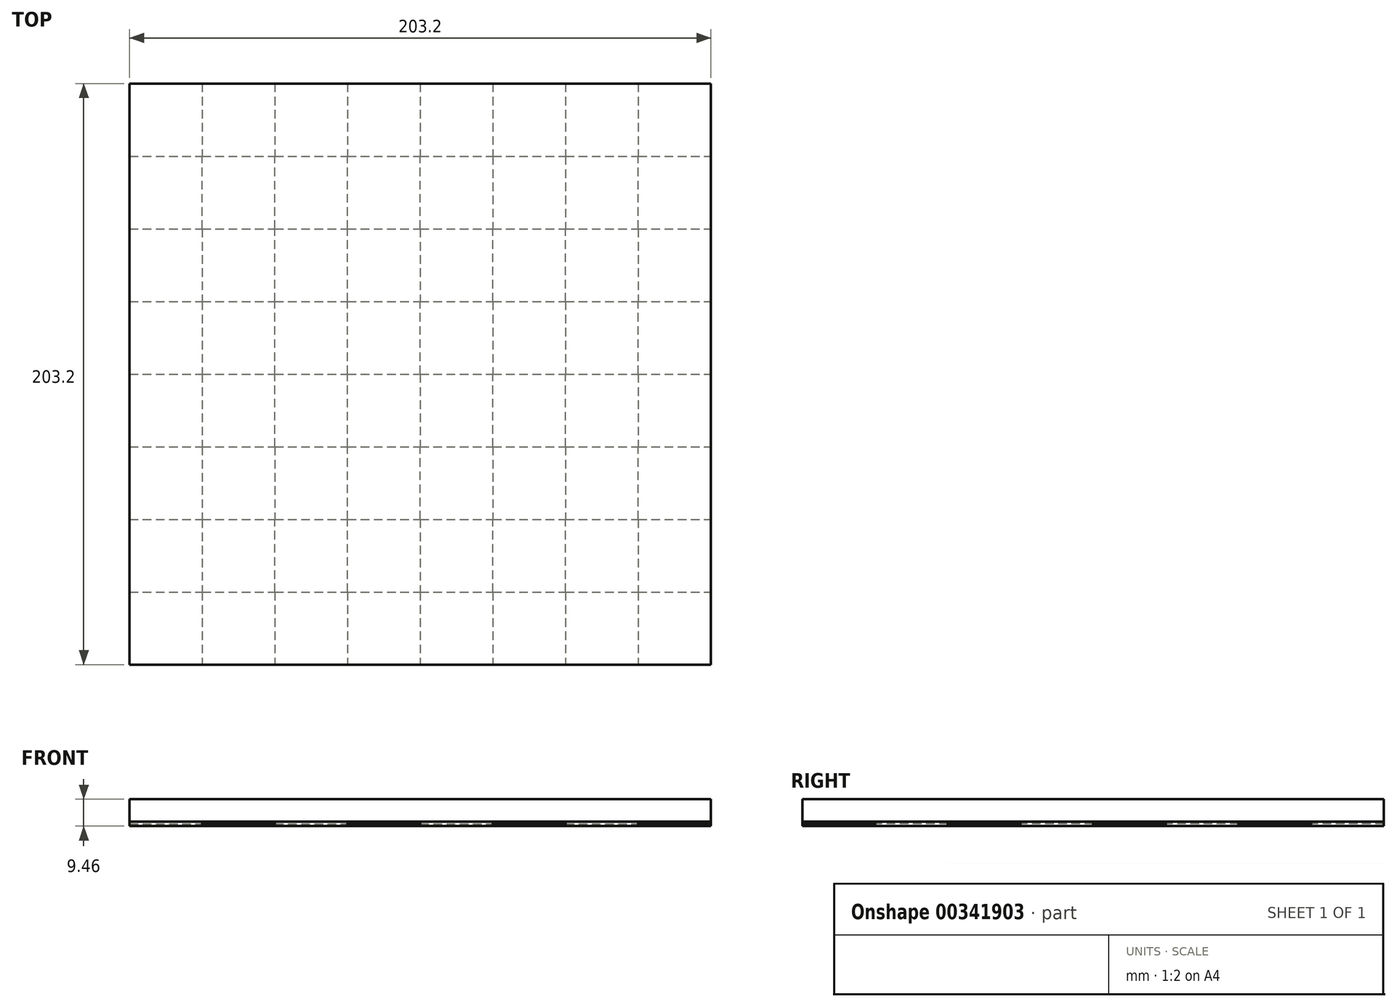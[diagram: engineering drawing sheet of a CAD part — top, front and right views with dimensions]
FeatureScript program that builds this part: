
annotation { "Feature Type Name" : "Feature", "Feature Type Description" : "" }
export const myFeature = defineFeature(function(context is Context, id is Id, definition is map)
    precondition{}
    {
        {
            var Q0;
            Q0=qCreatedBy(makeId("Top.planeOp"),FACE);
            var sketch = newSketch(context, id + "F0", { "sketchPlane" : qUnion([Q0])});
            skLineSegment(sketch, "E0.bottom", {"start": v(-101.6, -101.6) * mm, "end": v(101.6, -101.6) * mm});
            skLineSegment(sketch, "E0.top", {"start": v(-101.6, 101.6) * mm, "end": v(101.6, 101.6) * mm});
            skLineSegment(sketch, "E0.left", {"start": v(-101.6, -101.6) * mm, "end": v(-101.6, 101.6) * mm});
            skLineSegment(sketch, "E0.right", {"start": v(101.6, -101.6) * mm, "end": v(101.6, 101.6) * mm});
            skLineSegment(sketch, "E1.0", {"start": v(-76.2, -101.6) * mm, "end": v(-76.2, 101.6) * mm});
            skLineSegment(sketch, "E2.0", {"start": v(-50.8, -101.6) * mm, "end": v(-50.8, 101.6) * mm});
            skLineSegment(sketch, "E3.0", {"start": v(-25.4, -101.6) * mm, "end": v(-25.4, 101.6) * mm});
            skLineSegment(sketch, "E4.0", {"start": v(0, -101.6) * mm, "end": v(0, 101.6) * mm});
            skLineSegment(sketch, "E5.0", {"start": v(25.4, -101.6) * mm, "end": v(25.4, 101.6) * mm});
            skLineSegment(sketch, "E6.0", {"start": v(50.8, -101.6) * mm, "end": v(50.8, 101.6) * mm});
            skLineSegment(sketch, "E7.0", {"start": v(76.2, -101.6) * mm, "end": v(76.2, 101.6) * mm});
            skLineSegment(sketch, "E8.0", {"start": v(-101.6, 76.2) * mm, "end": v(101.6, 76.2) * mm});
            skLineSegment(sketch, "E9.0", {"start": v(-101.6, 50.8) * mm, "end": v(101.6, 50.8) * mm});
            skLineSegment(sketch, "E10.0", {"start": v(-101.6, 25.4) * mm, "end": v(101.6, 25.4) * mm});
            skLineSegment(sketch, "E11.0", {"start": v(-101.6, 0) * mm, "end": v(101.6, 0) * mm});
            skLineSegment(sketch, "E12.0", {"start": v(-101.6, -25.4) * mm, "end": v(101.6, -25.4) * mm});
            skLineSegment(sketch, "E13.0", {"start": v(-101.6, -50.8) * mm, "end": v(101.6, -50.8) * mm});
            skLineSegment(sketch, "E14.0", {"start": v(-101.6, -76.2) * mm, "end": v(101.6, -76.2) * mm});
            skSolve(sketch);
        }
        {
            var Q0;
            {var subQ0=sQuery(id+"F0.wireOp",EDGE,"E0.right");var subQ1=sQuery(id+"F0.wireOp",EDGE,"E0.top");var subQ2=makeQuery(id+"F0.imprint","INTERSECT",VERTEX,{"derivedFrom":[subQ1,subQ0]});Q0=makeQuery(id+"F0.imprint","IMPRINT",FACE,{"disambiguationData":[TD([[makeQuery(id+"F0.imprint","IMPRINT",EDGE,{"disambiguationData":[TD([[subQ2,1.0]])],"derivedFrom":subQ1}),-1.0]])]});}
            var Q1;
            {var subQ0=sQuery(id+"F0.wireOp",EDGE,"E9.0");var subQ1=sQuery(id+"F0.wireOp",EDGE,"E6.0");var subQ2=makeQuery(id+"F0.imprint","INTERSECT",VERTEX,{"derivedFrom":[subQ1,subQ0]});Q1=makeQuery(id+"F0.imprint","IMPRINT",FACE,{"disambiguationData":[TD([[makeQuery(id+"F0.imprint","IMPRINT",EDGE,{"disambiguationData":[TD([[subQ2,-1.0]])],"derivedFrom":subQ1}),-1.0]])]});}
            var Q2;
            {var subQ0=sQuery(id+"F0.wireOp",EDGE,"E5.0");var subQ1=sQuery(id+"F0.wireOp",EDGE,"E0.top");var subQ2=makeQuery(id+"F0.imprint","INTERSECT",VERTEX,{"derivedFrom":[subQ1,subQ0]});Q2=makeQuery(id+"F0.imprint","IMPRINT",FACE,{"disambiguationData":[TD([[makeQuery(id+"F0.imprint","IMPRINT",EDGE,{"disambiguationData":[TD([[subQ2,-1.0]])],"derivedFrom":subQ1}),-1.0]])]});}
            var Q3;
            {var subQ0=sQuery(id+"F0.wireOp",EDGE,"E3.0");var subQ1=sQuery(id+"F0.wireOp",EDGE,"E0.top");var subQ2=makeQuery(id+"F0.imprint","INTERSECT",VERTEX,{"derivedFrom":[subQ1,subQ0]});Q3=makeQuery(id+"F0.imprint","IMPRINT",FACE,{"disambiguationData":[TD([[makeQuery(id+"F0.imprint","IMPRINT",EDGE,{"disambiguationData":[TD([[subQ2,-1.0]])],"derivedFrom":subQ1}),-1.0]])]});}
            var Q4;
            {var subQ0=sQuery(id+"F0.wireOp",EDGE,"E9.0");var subQ1=sQuery(id+"F0.wireOp",EDGE,"E4.0");var subQ2=makeQuery(id+"F0.imprint","INTERSECT",VERTEX,{"derivedFrom":[subQ1,subQ0]});Q4=makeQuery(id+"F0.imprint","IMPRINT",FACE,{"disambiguationData":[TD([[makeQuery(id+"F0.imprint","IMPRINT",EDGE,{"disambiguationData":[TD([[subQ2,-1.0]])],"derivedFrom":subQ1}),-1.0]])]});}
            var Q5;
            {var subQ0=sQuery(id+"F0.wireOp",EDGE,"E1.0");var subQ1=sQuery(id+"F0.wireOp",EDGE,"E0.top");var subQ2=makeQuery(id+"F0.imprint","INTERSECT",VERTEX,{"derivedFrom":[subQ1,subQ0]});Q5=makeQuery(id+"F0.imprint","IMPRINT",FACE,{"disambiguationData":[TD([[makeQuery(id+"F0.imprint","IMPRINT",EDGE,{"disambiguationData":[TD([[subQ2,-1.0]])],"derivedFrom":subQ1}),-1.0]])]});}
            var Q6;
            {var subQ0=sQuery(id+"F0.wireOp",EDGE,"E8.0");var subQ1=sQuery(id+"F0.wireOp",EDGE,"E0.left");var subQ2=makeQuery(id+"F0.imprint","INTERSECT",VERTEX,{"derivedFrom":[subQ1,subQ0]});Q6=makeQuery(id+"F0.imprint","IMPRINT",FACE,{"disambiguationData":[TD([[makeQuery(id+"F0.imprint","IMPRINT",EDGE,{"disambiguationData":[TD([[subQ2,1.0]])],"derivedFrom":subQ1}),-1.0]])]});}
            var Q7;
            {var subQ0=sQuery(id+"F0.wireOp",EDGE,"E9.0");var subQ1=sQuery(id+"F0.wireOp",EDGE,"E2.0");var subQ2=makeQuery(id+"F0.imprint","INTERSECT",VERTEX,{"derivedFrom":[subQ1,subQ0]});Q7=makeQuery(id+"F0.imprint","IMPRINT",FACE,{"disambiguationData":[TD([[makeQuery(id+"F0.imprint","IMPRINT",EDGE,{"disambiguationData":[TD([[subQ2,-1.0]])],"derivedFrom":subQ1}),-1.0]])]});}
            var Q8;
            {var subQ0=sQuery(id+"F0.wireOp",EDGE,"E10.0");var subQ1=sQuery(id+"F0.wireOp",EDGE,"E1.0");var subQ2=makeQuery(id+"F0.imprint","INTERSECT",VERTEX,{"derivedFrom":[subQ1,subQ0]});Q8=makeQuery(id+"F0.imprint","IMPRINT",FACE,{"disambiguationData":[TD([[makeQuery(id+"F0.imprint","IMPRINT",EDGE,{"disambiguationData":[TD([[subQ2,-1.0]])],"derivedFrom":subQ1}),-1.0]])]});}
            var Q9;
            {var subQ0=sQuery(id+"F0.wireOp",EDGE,"E10.0");var subQ1=sQuery(id+"F0.wireOp",EDGE,"E0.left");var subQ2=makeQuery(id+"F0.imprint","INTERSECT",VERTEX,{"derivedFrom":[subQ1,subQ0]});Q9=makeQuery(id+"F0.imprint","IMPRINT",FACE,{"disambiguationData":[TD([[makeQuery(id+"F0.imprint","IMPRINT",EDGE,{"disambiguationData":[TD([[subQ2,1.0]])],"derivedFrom":subQ1}),-1.0]])]});}
            var Q10;
            {var subQ0=sQuery(id+"F0.wireOp",EDGE,"E12.0");var subQ1=sQuery(id+"F0.wireOp",EDGE,"E1.0");var subQ2=makeQuery(id+"F0.imprint","INTERSECT",VERTEX,{"derivedFrom":[subQ1,subQ0]});Q10=makeQuery(id+"F0.imprint","IMPRINT",FACE,{"disambiguationData":[TD([[makeQuery(id+"F0.imprint","IMPRINT",EDGE,{"disambiguationData":[TD([[subQ2,-1.0]])],"derivedFrom":subQ1}),-1.0]])]});}
            var Q11;
            {var subQ0=sQuery(id+"F0.wireOp",EDGE,"E12.0");var subQ1=sQuery(id+"F0.wireOp",EDGE,"E0.left");var subQ2=makeQuery(id+"F0.imprint","INTERSECT",VERTEX,{"derivedFrom":[subQ1,subQ0]});Q11=makeQuery(id+"F0.imprint","IMPRINT",FACE,{"disambiguationData":[TD([[makeQuery(id+"F0.imprint","IMPRINT",EDGE,{"disambiguationData":[TD([[subQ2,1.0]])],"derivedFrom":subQ1}),-1.0]])]});}
            var Q12;
            {var subQ0=sQuery(id+"F0.wireOp",EDGE,"E14.0");var subQ1=sQuery(id+"F0.wireOp",EDGE,"E1.0");var subQ2=makeQuery(id+"F0.imprint","INTERSECT",VERTEX,{"derivedFrom":[subQ1,subQ0]});Q12=makeQuery(id+"F0.imprint","IMPRINT",FACE,{"disambiguationData":[TD([[makeQuery(id+"F0.imprint","IMPRINT",EDGE,{"disambiguationData":[TD([[subQ2,-1.0]])],"derivedFrom":subQ1}),-1.0]])]});}
            var Q13;
            {var subQ0=sQuery(id+"F0.wireOp",EDGE,"E0.left");var subQ1=sQuery(id+"F0.wireOp",EDGE,"E0.bottom");var subQ2=makeQuery(id+"F0.imprint","INTERSECT",VERTEX,{"derivedFrom":[subQ1,subQ0]});Q13=makeQuery(id+"F0.imprint","IMPRINT",FACE,{"disambiguationData":[TD([[makeQuery(id+"F0.imprint","IMPRINT",EDGE,{"disambiguationData":[TD([[subQ2,-1.0]])],"derivedFrom":subQ1}),1.0]])]});}
            var Q14;
            {var subQ0=sQuery(id+"F0.wireOp",EDGE,"E2.0");var subQ1=sQuery(id+"F0.wireOp",EDGE,"E0.bottom");var subQ2=makeQuery(id+"F0.imprint","INTERSECT",VERTEX,{"derivedFrom":[subQ1,subQ0]});Q14=makeQuery(id+"F0.imprint","IMPRINT",FACE,{"disambiguationData":[TD([[makeQuery(id+"F0.imprint","IMPRINT",EDGE,{"disambiguationData":[TD([[subQ2,-1.0]])],"derivedFrom":subQ1}),1.0]])]});}
            var Q15;
            {var subQ0=sQuery(id+"F0.wireOp",EDGE,"E13.0");var subQ1=sQuery(id+"F0.wireOp",EDGE,"E2.0");var subQ2=makeQuery(id+"F0.imprint","INTERSECT",VERTEX,{"derivedFrom":[subQ1,subQ0]});Q15=makeQuery(id+"F0.imprint","IMPRINT",FACE,{"disambiguationData":[TD([[makeQuery(id+"F0.imprint","IMPRINT",EDGE,{"disambiguationData":[TD([[subQ2,-1.0]])],"derivedFrom":subQ1}),-1.0]])]});}
            var Q16;
            {var subQ0=sQuery(id+"F0.wireOp",EDGE,"E11.0");var subQ1=sQuery(id+"F0.wireOp",EDGE,"E2.0");var subQ2=makeQuery(id+"F0.imprint","INTERSECT",VERTEX,{"derivedFrom":[subQ1,subQ0]});Q16=makeQuery(id+"F0.imprint","IMPRINT",FACE,{"disambiguationData":[TD([[makeQuery(id+"F0.imprint","IMPRINT",EDGE,{"disambiguationData":[TD([[subQ2,-1.0]])],"derivedFrom":subQ1}),-1.0]])]});}
            var Q17;
            {var subQ0=sQuery(id+"F0.wireOp",EDGE,"E10.0");var subQ1=sQuery(id+"F0.wireOp",EDGE,"E3.0");var subQ2=makeQuery(id+"F0.imprint","INTERSECT",VERTEX,{"derivedFrom":[subQ1,subQ0]});Q17=makeQuery(id+"F0.imprint","IMPRINT",FACE,{"disambiguationData":[TD([[makeQuery(id+"F0.imprint","IMPRINT",EDGE,{"disambiguationData":[TD([[subQ2,-1.0]])],"derivedFrom":subQ1}),-1.0]])]});}
            var Q18;
            {var subQ0=sQuery(id+"F0.wireOp",EDGE,"E12.0");var subQ1=sQuery(id+"F0.wireOp",EDGE,"E3.0");var subQ2=makeQuery(id+"F0.imprint","INTERSECT",VERTEX,{"derivedFrom":[subQ1,subQ0]});Q18=makeQuery(id+"F0.imprint","IMPRINT",FACE,{"disambiguationData":[TD([[makeQuery(id+"F0.imprint","IMPRINT",EDGE,{"disambiguationData":[TD([[subQ2,-1.0]])],"derivedFrom":subQ1}),-1.0]])]});}
            var Q19;
            {var subQ0=sQuery(id+"F0.wireOp",EDGE,"E14.0");var subQ1=sQuery(id+"F0.wireOp",EDGE,"E3.0");var subQ2=makeQuery(id+"F0.imprint","INTERSECT",VERTEX,{"derivedFrom":[subQ1,subQ0]});Q19=makeQuery(id+"F0.imprint","IMPRINT",FACE,{"disambiguationData":[TD([[makeQuery(id+"F0.imprint","IMPRINT",EDGE,{"disambiguationData":[TD([[subQ2,-1.0]])],"derivedFrom":subQ1}),-1.0]])]});}
            var Q20;
            {var subQ0=sQuery(id+"F0.wireOp",EDGE,"E4.0");var subQ1=sQuery(id+"F0.wireOp",EDGE,"E0.bottom");var subQ2=makeQuery(id+"F0.imprint","INTERSECT",VERTEX,{"derivedFrom":[subQ1,subQ0]});Q20=makeQuery(id+"F0.imprint","IMPRINT",FACE,{"disambiguationData":[TD([[makeQuery(id+"F0.imprint","IMPRINT",EDGE,{"disambiguationData":[TD([[subQ2,-1.0]])],"derivedFrom":subQ1}),1.0]])]});}
            var Q21;
            {var subQ0=sQuery(id+"F0.wireOp",EDGE,"E11.0");var subQ1=sQuery(id+"F0.wireOp",EDGE,"E4.0");var subQ2=makeQuery(id+"F0.imprint","INTERSECT",VERTEX,{"derivedFrom":[subQ1,subQ0]});Q21=makeQuery(id+"F0.imprint","IMPRINT",FACE,{"disambiguationData":[TD([[makeQuery(id+"F0.imprint","IMPRINT",EDGE,{"disambiguationData":[TD([[subQ2,-1.0]])],"derivedFrom":subQ1}),-1.0]])]});}
            var Q22;
            {var subQ0=sQuery(id+"F0.wireOp",EDGE,"E10.0");var subQ1=sQuery(id+"F0.wireOp",EDGE,"E5.0");var subQ2=makeQuery(id+"F0.imprint","INTERSECT",VERTEX,{"derivedFrom":[subQ1,subQ0]});Q22=makeQuery(id+"F0.imprint","IMPRINT",FACE,{"disambiguationData":[TD([[makeQuery(id+"F0.imprint","IMPRINT",EDGE,{"disambiguationData":[TD([[subQ2,-1.0]])],"derivedFrom":subQ1}),-1.0]])]});}
            var Q23;
            {var subQ0=sQuery(id+"F0.wireOp",EDGE,"E12.0");var subQ1=sQuery(id+"F0.wireOp",EDGE,"E5.0");var subQ2=makeQuery(id+"F0.imprint","INTERSECT",VERTEX,{"derivedFrom":[subQ1,subQ0]});Q23=makeQuery(id+"F0.imprint","IMPRINT",FACE,{"disambiguationData":[TD([[makeQuery(id+"F0.imprint","IMPRINT",EDGE,{"disambiguationData":[TD([[subQ2,-1.0]])],"derivedFrom":subQ1}),-1.0]])]});}
            var Q24;
            {var subQ0=sQuery(id+"F0.wireOp",EDGE,"E13.0");var subQ1=sQuery(id+"F0.wireOp",EDGE,"E4.0");var subQ2=makeQuery(id+"F0.imprint","INTERSECT",VERTEX,{"derivedFrom":[subQ1,subQ0]});Q24=makeQuery(id+"F0.imprint","IMPRINT",FACE,{"disambiguationData":[TD([[makeQuery(id+"F0.imprint","IMPRINT",EDGE,{"disambiguationData":[TD([[subQ2,-1.0]])],"derivedFrom":subQ1}),-1.0]])]});}
            var Q25;
            {var subQ0=sQuery(id+"F0.wireOp",EDGE,"E14.0");var subQ1=sQuery(id+"F0.wireOp",EDGE,"E5.0");var subQ2=makeQuery(id+"F0.imprint","INTERSECT",VERTEX,{"derivedFrom":[subQ1,subQ0]});Q25=makeQuery(id+"F0.imprint","IMPRINT",FACE,{"disambiguationData":[TD([[makeQuery(id+"F0.imprint","IMPRINT",EDGE,{"disambiguationData":[TD([[subQ2,-1.0]])],"derivedFrom":subQ1}),-1.0]])]});}
            var Q26;
            {var subQ0=sQuery(id+"F0.wireOp",EDGE,"E6.0");var subQ1=sQuery(id+"F0.wireOp",EDGE,"E0.bottom");var subQ2=makeQuery(id+"F0.imprint","INTERSECT",VERTEX,{"derivedFrom":[subQ1,subQ0]});Q26=makeQuery(id+"F0.imprint","IMPRINT",FACE,{"disambiguationData":[TD([[makeQuery(id+"F0.imprint","IMPRINT",EDGE,{"disambiguationData":[TD([[subQ2,-1.0]])],"derivedFrom":subQ1}),1.0]])]});}
            var Q27;
            {var subQ0=sQuery(id+"F0.wireOp",EDGE,"E13.0");var subQ1=sQuery(id+"F0.wireOp",EDGE,"E0.right");var subQ2=makeQuery(id+"F0.imprint","INTERSECT",VERTEX,{"derivedFrom":[subQ1,subQ0]});Q27=makeQuery(id+"F0.imprint","IMPRINT",FACE,{"disambiguationData":[TD([[makeQuery(id+"F0.imprint","IMPRINT",EDGE,{"disambiguationData":[TD([[subQ2,1.0]])],"derivedFrom":subQ1}),1.0]])]});}
            var Q28;
            {var subQ0=sQuery(id+"F0.wireOp",EDGE,"E13.0");var subQ1=sQuery(id+"F0.wireOp",EDGE,"E6.0");var subQ2=makeQuery(id+"F0.imprint","INTERSECT",VERTEX,{"derivedFrom":[subQ1,subQ0]});Q28=makeQuery(id+"F0.imprint","IMPRINT",FACE,{"disambiguationData":[TD([[makeQuery(id+"F0.imprint","IMPRINT",EDGE,{"disambiguationData":[TD([[subQ2,-1.0]])],"derivedFrom":subQ1}),-1.0]])]});}
            var Q29;
            {var subQ0=sQuery(id+"F0.wireOp",EDGE,"E11.0");var subQ1=sQuery(id+"F0.wireOp",EDGE,"E0.right");var subQ2=makeQuery(id+"F0.imprint","INTERSECT",VERTEX,{"derivedFrom":[subQ1,subQ0]});Q29=makeQuery(id+"F0.imprint","IMPRINT",FACE,{"disambiguationData":[TD([[makeQuery(id+"F0.imprint","IMPRINT",EDGE,{"disambiguationData":[TD([[subQ2,1.0]])],"derivedFrom":subQ1}),1.0]])]});}
            var Q30;
            {var subQ0=sQuery(id+"F0.wireOp",EDGE,"E11.0");var subQ1=sQuery(id+"F0.wireOp",EDGE,"E6.0");var subQ2=makeQuery(id+"F0.imprint","INTERSECT",VERTEX,{"derivedFrom":[subQ1,subQ0]});Q30=makeQuery(id+"F0.imprint","IMPRINT",FACE,{"disambiguationData":[TD([[makeQuery(id+"F0.imprint","IMPRINT",EDGE,{"disambiguationData":[TD([[subQ2,-1.0]])],"derivedFrom":subQ1}),-1.0]])]});}
            var Q31;
            {var subQ0=sQuery(id+"F0.wireOp",EDGE,"E9.0");var subQ1=sQuery(id+"F0.wireOp",EDGE,"E0.right");var subQ2=makeQuery(id+"F0.imprint","INTERSECT",VERTEX,{"derivedFrom":[subQ1,subQ0]});Q31=makeQuery(id+"F0.imprint","IMPRINT",FACE,{"disambiguationData":[TD([[makeQuery(id+"F0.imprint","IMPRINT",EDGE,{"disambiguationData":[TD([[subQ2,1.0]])],"derivedFrom":subQ1}),1.0]])]});}
            extrude(context, id + "F1", {"entities" : qUnion([Q0, Q1, Q2, Q3, Q4, Q5, Q6, Q7, Q8, Q9, Q10, Q11, Q12, Q13, Q14, Q15, Q16, Q17, Q18, Q19, Q20, Q21, Q22, Q23, Q24, Q25, Q26, Q27, Q28, Q29, Q30, Q31]), "oppositeDirection" : true, "depth" : 1.52 * mm});
        }
        {
            var Q0;
            Q0=qCreatedBy(makeId("Top.planeOp"),FACE);
            var sketch = newSketch(context, id + "F2", { "sketchPlane" : qUnion([Q0])});
            skLineSegment(sketch, "E15.bottom", {"start": v(-101.6, 101.6) * mm, "end": v(101.6, 101.6) * mm});
            skLineSegment(sketch, "E15.top", {"start": v(-101.6, -101.6) * mm, "end": v(101.6, -101.6) * mm});
            skLineSegment(sketch, "E15.left", {"start": v(-101.6, 101.6) * mm, "end": v(-101.6, -101.6) * mm});
            skLineSegment(sketch, "E15.right", {"start": v(101.6, 101.6) * mm, "end": v(101.6, -101.6) * mm});
            skSolve(sketch);
        }
        {
            var Q0;
            Q0=makeQuery(id+"F2.imprint","IMPRINT",FACE,{"disambiguationData":[TD([[makeQuery(id+"F2.imprint","IMPRINT",EDGE,{"derivedFrom":sQuery(id+"F2.wireOp",EDGE,"E15.bottom")}),-1.0]])]});
            extrude(context, id + "F3", {"entities" : qUnion([Q0]), "depth" : 7.94 * mm});
        }
        {
            var Q0;
            Q0=makeQuery(id+"F3.opExtrude","CAP_FACE",FACE,{"disambiguationData":[OSD([sQuery(id+"F2.wireOp",EDGE,"E15.bottom"),sQuery(id+"F2.wireOp",EDGE,"E15.top"),sQuery(id+"F2.wireOp",EDGE,"E15.left"),sQuery(id+"F2.wireOp",EDGE,"E15.right")])],"isStart":true});
            var sketch = newSketch(context, id + "F4", { "sketchPlane" : qUnion([Q0])});
            skLineSegment(sketch, "E16.bottom", {"start": v(-101.6, -101.6) * mm, "end": v(101.6, -101.6) * mm});
            skLineSegment(sketch, "E16.top", {"start": v(-101.6, 101.6) * mm, "end": v(101.6, 101.6) * mm});
            skLineSegment(sketch, "E16.left", {"start": v(-101.6, -101.6) * mm, "end": v(-101.6, 101.6) * mm});
            skLineSegment(sketch, "E16.right", {"start": v(101.6, -101.6) * mm, "end": v(101.6, 101.6) * mm});
            skLineSegment(sketch, "E17.0", {"start": v(-76.2, -101.6) * mm, "end": v(-76.2, 101.6) * mm});
            skLineSegment(sketch, "E18.0", {"start": v(-50.8, -101.6) * mm, "end": v(-50.8, 101.6) * mm});
            skLineSegment(sketch, "E19.0", {"start": v(-25.4, -101.6) * mm, "end": v(-25.4, 101.6) * mm});
            skLineSegment(sketch, "E20.0", {"start": v(0, -101.6) * mm, "end": v(0, 101.6) * mm});
            skLineSegment(sketch, "E21.0", {"start": v(25.4, -101.6) * mm, "end": v(25.4, 101.6) * mm});
            skLineSegment(sketch, "E22.0", {"start": v(50.8, -101.6) * mm, "end": v(50.8, 101.6) * mm});
            skLineSegment(sketch, "E23.0", {"start": v(76.2, -101.6) * mm, "end": v(76.2, 101.6) * mm});
            skLineSegment(sketch, "E24.0", {"start": v(-101.6, 76.2) * mm, "end": v(101.6, 76.2) * mm});
            skLineSegment(sketch, "E25.0", {"start": v(-101.6, 50.8) * mm, "end": v(101.6, 50.8) * mm});
            skLineSegment(sketch, "E26.0", {"start": v(-101.6, 25.4) * mm, "end": v(101.6, 25.4) * mm});
            skLineSegment(sketch, "E27.0", {"start": v(-101.6, 0) * mm, "end": v(101.6, 0) * mm});
            skLineSegment(sketch, "E28.0", {"start": v(-101.6, -25.4) * mm, "end": v(101.6, -25.4) * mm});
            skLineSegment(sketch, "E29.0", {"start": v(-101.6, -50.8) * mm, "end": v(101.6, -50.8) * mm});
            skLineSegment(sketch, "E30.0", {"start": v(-101.6, -76.2) * mm, "end": v(101.6, -76.2) * mm});
            skSolve(sketch);
        }
        {
            var Q0;
            {var subQ0=sQuery(id+"F4.wireOp",EDGE,"E17.0");var subQ1=sQuery(id+"F4.wireOp",EDGE,"E16.top");var subQ2=makeQuery(id+"F4.imprint","INTERSECT",VERTEX,{"derivedFrom":[subQ1,subQ0]});Q0=makeQuery(id+"F4.imprint","IMPRINT",FACE,{"disambiguationData":[TD([[makeQuery(id+"F4.imprint","IMPRINT",EDGE,{"disambiguationData":[TD([[subQ2,-1.0]])],"derivedFrom":subQ1}),-1.0]])]});}
            var Q1;
            {var subQ0=sQuery(id+"F4.wireOp",EDGE,"E19.0");var subQ1=sQuery(id+"F4.wireOp",EDGE,"E16.top");var subQ2=makeQuery(id+"F4.imprint","INTERSECT",VERTEX,{"derivedFrom":[subQ1,subQ0]});Q1=makeQuery(id+"F4.imprint","IMPRINT",FACE,{"disambiguationData":[TD([[makeQuery(id+"F4.imprint","IMPRINT",EDGE,{"disambiguationData":[TD([[subQ2,-1.0]])],"derivedFrom":subQ1}),-1.0]])]});}
            var Q2;
            {var subQ0=sQuery(id+"F4.wireOp",EDGE,"E21.0");var subQ1=sQuery(id+"F4.wireOp",EDGE,"E16.top");var subQ2=makeQuery(id+"F4.imprint","INTERSECT",VERTEX,{"derivedFrom":[subQ1,subQ0]});Q2=makeQuery(id+"F4.imprint","IMPRINT",FACE,{"disambiguationData":[TD([[makeQuery(id+"F4.imprint","IMPRINT",EDGE,{"disambiguationData":[TD([[subQ2,-1.0]])],"derivedFrom":subQ1}),-1.0]])]});}
            var Q3;
            {var subQ0=sQuery(id+"F4.wireOp",EDGE,"E16.right");var subQ1=sQuery(id+"F4.wireOp",EDGE,"E16.top");var subQ2=makeQuery(id+"F4.imprint","INTERSECT",VERTEX,{"derivedFrom":[subQ1,subQ0]});Q3=makeQuery(id+"F4.imprint","IMPRINT",FACE,{"disambiguationData":[TD([[makeQuery(id+"F4.imprint","IMPRINT",EDGE,{"disambiguationData":[TD([[subQ2,1.0]])],"derivedFrom":subQ1}),-1.0]])]});}
            var Q4;
            {var subQ0=sQuery(id+"F4.wireOp",EDGE,"E24.0");var subQ1=sQuery(id+"F4.wireOp",EDGE,"E16.left");var subQ2=makeQuery(id+"F4.imprint","INTERSECT",VERTEX,{"derivedFrom":[subQ1,subQ0]});Q4=makeQuery(id+"F4.imprint","IMPRINT",FACE,{"disambiguationData":[TD([[makeQuery(id+"F4.imprint","IMPRINT",EDGE,{"disambiguationData":[TD([[subQ2,1.0]])],"derivedFrom":subQ1}),-1.0]])]});}
            var Q5;
            {var subQ0=sQuery(id+"F4.wireOp",EDGE,"E25.0");var subQ1=sQuery(id+"F4.wireOp",EDGE,"E18.0");var subQ2=makeQuery(id+"F4.imprint","INTERSECT",VERTEX,{"derivedFrom":[subQ1,subQ0]});Q5=makeQuery(id+"F4.imprint","IMPRINT",FACE,{"disambiguationData":[TD([[makeQuery(id+"F4.imprint","IMPRINT",EDGE,{"disambiguationData":[TD([[subQ2,-1.0]])],"derivedFrom":subQ1}),-1.0]])]});}
            var Q6;
            {var subQ0=sQuery(id+"F4.wireOp",EDGE,"E25.0");var subQ1=sQuery(id+"F4.wireOp",EDGE,"E20.0");var subQ2=makeQuery(id+"F4.imprint","INTERSECT",VERTEX,{"derivedFrom":[subQ1,subQ0]});Q6=makeQuery(id+"F4.imprint","IMPRINT",FACE,{"disambiguationData":[TD([[makeQuery(id+"F4.imprint","IMPRINT",EDGE,{"disambiguationData":[TD([[subQ2,-1.0]])],"derivedFrom":subQ1}),-1.0]])]});}
            var Q7;
            {var subQ0=sQuery(id+"F4.wireOp",EDGE,"E25.0");var subQ1=sQuery(id+"F4.wireOp",EDGE,"E16.right");var subQ2=makeQuery(id+"F4.imprint","INTERSECT",VERTEX,{"derivedFrom":[subQ1,subQ0]});Q7=makeQuery(id+"F4.imprint","IMPRINT",FACE,{"disambiguationData":[TD([[makeQuery(id+"F4.imprint","IMPRINT",EDGE,{"disambiguationData":[TD([[subQ2,1.0]])],"derivedFrom":subQ1}),1.0]])]});}
            var Q8;
            {var subQ0=sQuery(id+"F4.wireOp",EDGE,"E27.0");var subQ1=sQuery(id+"F4.wireOp",EDGE,"E22.0");var subQ2=makeQuery(id+"F4.imprint","INTERSECT",VERTEX,{"derivedFrom":[subQ1,subQ0]});Q8=makeQuery(id+"F4.imprint","IMPRINT",FACE,{"disambiguationData":[TD([[makeQuery(id+"F4.imprint","IMPRINT",EDGE,{"disambiguationData":[TD([[subQ2,-1.0]])],"derivedFrom":subQ1}),-1.0]])]});}
            var Q9;
            {var subQ0=sQuery(id+"F4.wireOp",EDGE,"E26.0");var subQ1=sQuery(id+"F4.wireOp",EDGE,"E21.0");var subQ2=makeQuery(id+"F4.imprint","INTERSECT",VERTEX,{"derivedFrom":[subQ1,subQ0]});Q9=makeQuery(id+"F4.imprint","IMPRINT",FACE,{"disambiguationData":[TD([[makeQuery(id+"F4.imprint","IMPRINT",EDGE,{"disambiguationData":[TD([[subQ2,-1.0]])],"derivedFrom":subQ1}),-1.0]])]});}
            var Q10;
            {var subQ0=sQuery(id+"F4.wireOp",EDGE,"E25.0");var subQ1=sQuery(id+"F4.wireOp",EDGE,"E22.0");var subQ2=makeQuery(id+"F4.imprint","INTERSECT",VERTEX,{"derivedFrom":[subQ1,subQ0]});Q10=makeQuery(id+"F4.imprint","IMPRINT",FACE,{"disambiguationData":[TD([[makeQuery(id+"F4.imprint","IMPRINT",EDGE,{"disambiguationData":[TD([[subQ2,-1.0]])],"derivedFrom":subQ1}),-1.0]])]});}
            var Q11;
            {var subQ0=sQuery(id+"F4.wireOp",EDGE,"E26.0");var subQ1=sQuery(id+"F4.wireOp",EDGE,"E19.0");var subQ2=makeQuery(id+"F4.imprint","INTERSECT",VERTEX,{"derivedFrom":[subQ1,subQ0]});Q11=makeQuery(id+"F4.imprint","IMPRINT",FACE,{"disambiguationData":[TD([[makeQuery(id+"F4.imprint","IMPRINT",EDGE,{"disambiguationData":[TD([[subQ2,-1.0]])],"derivedFrom":subQ1}),-1.0]])]});}
            var Q12;
            {var subQ0=sQuery(id+"F4.wireOp",EDGE,"E26.0");var subQ1=sQuery(id+"F4.wireOp",EDGE,"E17.0");var subQ2=makeQuery(id+"F4.imprint","INTERSECT",VERTEX,{"derivedFrom":[subQ1,subQ0]});Q12=makeQuery(id+"F4.imprint","IMPRINT",FACE,{"disambiguationData":[TD([[makeQuery(id+"F4.imprint","IMPRINT",EDGE,{"disambiguationData":[TD([[subQ2,-1.0]])],"derivedFrom":subQ1}),-1.0]])]});}
            var Q13;
            {var subQ0=sQuery(id+"F4.wireOp",EDGE,"E26.0");var subQ1=sQuery(id+"F4.wireOp",EDGE,"E16.left");var subQ2=makeQuery(id+"F4.imprint","INTERSECT",VERTEX,{"derivedFrom":[subQ1,subQ0]});Q13=makeQuery(id+"F4.imprint","IMPRINT",FACE,{"disambiguationData":[TD([[makeQuery(id+"F4.imprint","IMPRINT",EDGE,{"disambiguationData":[TD([[subQ2,1.0]])],"derivedFrom":subQ1}),-1.0]])]});}
            var Q14;
            {var subQ0=sQuery(id+"F4.wireOp",EDGE,"E27.0");var subQ1=sQuery(id+"F4.wireOp",EDGE,"E18.0");var subQ2=makeQuery(id+"F4.imprint","INTERSECT",VERTEX,{"derivedFrom":[subQ1,subQ0]});Q14=makeQuery(id+"F4.imprint","IMPRINT",FACE,{"disambiguationData":[TD([[makeQuery(id+"F4.imprint","IMPRINT",EDGE,{"disambiguationData":[TD([[subQ2,-1.0]])],"derivedFrom":subQ1}),-1.0]])]});}
            var Q15;
            {var subQ0=sQuery(id+"F4.wireOp",EDGE,"E27.0");var subQ1=sQuery(id+"F4.wireOp",EDGE,"E20.0");var subQ2=makeQuery(id+"F4.imprint","INTERSECT",VERTEX,{"derivedFrom":[subQ1,subQ0]});Q15=makeQuery(id+"F4.imprint","IMPRINT",FACE,{"disambiguationData":[TD([[makeQuery(id+"F4.imprint","IMPRINT",EDGE,{"disambiguationData":[TD([[subQ2,-1.0]])],"derivedFrom":subQ1}),-1.0]])]});}
            var Q16;
            {var subQ0=sQuery(id+"F4.wireOp",EDGE,"E27.0");var subQ1=sQuery(id+"F4.wireOp",EDGE,"E16.right");var subQ2=makeQuery(id+"F4.imprint","INTERSECT",VERTEX,{"derivedFrom":[subQ1,subQ0]});Q16=makeQuery(id+"F4.imprint","IMPRINT",FACE,{"disambiguationData":[TD([[makeQuery(id+"F4.imprint","IMPRINT",EDGE,{"disambiguationData":[TD([[subQ2,1.0]])],"derivedFrom":subQ1}),1.0]])]});}
            var Q17;
            {var subQ0=sQuery(id+"F4.wireOp",EDGE,"E28.0");var subQ1=sQuery(id+"F4.wireOp",EDGE,"E21.0");var subQ2=makeQuery(id+"F4.imprint","INTERSECT",VERTEX,{"derivedFrom":[subQ1,subQ0]});Q17=makeQuery(id+"F4.imprint","IMPRINT",FACE,{"disambiguationData":[TD([[makeQuery(id+"F4.imprint","IMPRINT",EDGE,{"disambiguationData":[TD([[subQ2,-1.0]])],"derivedFrom":subQ1}),-1.0]])]});}
            var Q18;
            {var subQ0=sQuery(id+"F4.wireOp",EDGE,"E28.0");var subQ1=sQuery(id+"F4.wireOp",EDGE,"E19.0");var subQ2=makeQuery(id+"F4.imprint","INTERSECT",VERTEX,{"derivedFrom":[subQ1,subQ0]});Q18=makeQuery(id+"F4.imprint","IMPRINT",FACE,{"disambiguationData":[TD([[makeQuery(id+"F4.imprint","IMPRINT",EDGE,{"disambiguationData":[TD([[subQ2,-1.0]])],"derivedFrom":subQ1}),-1.0]])]});}
            var Q19;
            {var subQ0=sQuery(id+"F4.wireOp",EDGE,"E28.0");var subQ1=sQuery(id+"F4.wireOp",EDGE,"E17.0");var subQ2=makeQuery(id+"F4.imprint","INTERSECT",VERTEX,{"derivedFrom":[subQ1,subQ0]});Q19=makeQuery(id+"F4.imprint","IMPRINT",FACE,{"disambiguationData":[TD([[makeQuery(id+"F4.imprint","IMPRINT",EDGE,{"disambiguationData":[TD([[subQ2,-1.0]])],"derivedFrom":subQ1}),-1.0]])]});}
            var Q20;
            {var subQ0=sQuery(id+"F4.wireOp",EDGE,"E28.0");var subQ1=sQuery(id+"F4.wireOp",EDGE,"E16.left");var subQ2=makeQuery(id+"F4.imprint","INTERSECT",VERTEX,{"derivedFrom":[subQ1,subQ0]});Q20=makeQuery(id+"F4.imprint","IMPRINT",FACE,{"disambiguationData":[TD([[makeQuery(id+"F4.imprint","IMPRINT",EDGE,{"disambiguationData":[TD([[subQ2,1.0]])],"derivedFrom":subQ1}),-1.0]])]});}
            var Q21;
            {var subQ0=sQuery(id+"F4.wireOp",EDGE,"E29.0");var subQ1=sQuery(id+"F4.wireOp",EDGE,"E18.0");var subQ2=makeQuery(id+"F4.imprint","INTERSECT",VERTEX,{"derivedFrom":[subQ1,subQ0]});Q21=makeQuery(id+"F4.imprint","IMPRINT",FACE,{"disambiguationData":[TD([[makeQuery(id+"F4.imprint","IMPRINT",EDGE,{"disambiguationData":[TD([[subQ2,-1.0]])],"derivedFrom":subQ1}),-1.0]])]});}
            var Q22;
            {var subQ0=sQuery(id+"F4.wireOp",EDGE,"E29.0");var subQ1=sQuery(id+"F4.wireOp",EDGE,"E20.0");var subQ2=makeQuery(id+"F4.imprint","INTERSECT",VERTEX,{"derivedFrom":[subQ1,subQ0]});Q22=makeQuery(id+"F4.imprint","IMPRINT",FACE,{"disambiguationData":[TD([[makeQuery(id+"F4.imprint","IMPRINT",EDGE,{"disambiguationData":[TD([[subQ2,-1.0]])],"derivedFrom":subQ1}),-1.0]])]});}
            var Q23;
            {var subQ0=sQuery(id+"F4.wireOp",EDGE,"E29.0");var subQ1=sQuery(id+"F4.wireOp",EDGE,"E22.0");var subQ2=makeQuery(id+"F4.imprint","INTERSECT",VERTEX,{"derivedFrom":[subQ1,subQ0]});Q23=makeQuery(id+"F4.imprint","IMPRINT",FACE,{"disambiguationData":[TD([[makeQuery(id+"F4.imprint","IMPRINT",EDGE,{"disambiguationData":[TD([[subQ2,-1.0]])],"derivedFrom":subQ1}),-1.0]])]});}
            var Q24;
            {var subQ0=sQuery(id+"F4.wireOp",EDGE,"E29.0");var subQ1=sQuery(id+"F4.wireOp",EDGE,"E16.right");var subQ2=makeQuery(id+"F4.imprint","INTERSECT",VERTEX,{"derivedFrom":[subQ1,subQ0]});Q24=makeQuery(id+"F4.imprint","IMPRINT",FACE,{"disambiguationData":[TD([[makeQuery(id+"F4.imprint","IMPRINT",EDGE,{"disambiguationData":[TD([[subQ2,1.0]])],"derivedFrom":subQ1}),1.0]])]});}
            var Q25;
            {var subQ0=sQuery(id+"F4.wireOp",EDGE,"E22.0");var subQ1=sQuery(id+"F4.wireOp",EDGE,"E16.bottom");var subQ2=makeQuery(id+"F4.imprint","INTERSECT",VERTEX,{"derivedFrom":[subQ1,subQ0]});Q25=makeQuery(id+"F4.imprint","IMPRINT",FACE,{"disambiguationData":[TD([[makeQuery(id+"F4.imprint","IMPRINT",EDGE,{"disambiguationData":[TD([[subQ2,-1.0]])],"derivedFrom":subQ1}),1.0]])]});}
            var Q26;
            {var subQ0=sQuery(id+"F4.wireOp",EDGE,"E30.0");var subQ1=sQuery(id+"F4.wireOp",EDGE,"E21.0");var subQ2=makeQuery(id+"F4.imprint","INTERSECT",VERTEX,{"derivedFrom":[subQ1,subQ0]});Q26=makeQuery(id+"F4.imprint","IMPRINT",FACE,{"disambiguationData":[TD([[makeQuery(id+"F4.imprint","IMPRINT",EDGE,{"disambiguationData":[TD([[subQ2,-1.0]])],"derivedFrom":subQ1}),-1.0]])]});}
            var Q27;
            {var subQ0=sQuery(id+"F4.wireOp",EDGE,"E20.0");var subQ1=sQuery(id+"F4.wireOp",EDGE,"E16.bottom");var subQ2=makeQuery(id+"F4.imprint","INTERSECT",VERTEX,{"derivedFrom":[subQ1,subQ0]});Q27=makeQuery(id+"F4.imprint","IMPRINT",FACE,{"disambiguationData":[TD([[makeQuery(id+"F4.imprint","IMPRINT",EDGE,{"disambiguationData":[TD([[subQ2,-1.0]])],"derivedFrom":subQ1}),1.0]])]});}
            var Q28;
            {var subQ0=sQuery(id+"F4.wireOp",EDGE,"E30.0");var subQ1=sQuery(id+"F4.wireOp",EDGE,"E19.0");var subQ2=makeQuery(id+"F4.imprint","INTERSECT",VERTEX,{"derivedFrom":[subQ1,subQ0]});Q28=makeQuery(id+"F4.imprint","IMPRINT",FACE,{"disambiguationData":[TD([[makeQuery(id+"F4.imprint","IMPRINT",EDGE,{"disambiguationData":[TD([[subQ2,-1.0]])],"derivedFrom":subQ1}),-1.0]])]});}
            var Q29;
            {var subQ0=sQuery(id+"F4.wireOp",EDGE,"E18.0");var subQ1=sQuery(id+"F4.wireOp",EDGE,"E16.bottom");var subQ2=makeQuery(id+"F4.imprint","INTERSECT",VERTEX,{"derivedFrom":[subQ1,subQ0]});Q29=makeQuery(id+"F4.imprint","IMPRINT",FACE,{"disambiguationData":[TD([[makeQuery(id+"F4.imprint","IMPRINT",EDGE,{"disambiguationData":[TD([[subQ2,-1.0]])],"derivedFrom":subQ1}),1.0]])]});}
            var Q30;
            {var subQ0=sQuery(id+"F4.wireOp",EDGE,"E30.0");var subQ1=sQuery(id+"F4.wireOp",EDGE,"E17.0");var subQ2=makeQuery(id+"F4.imprint","INTERSECT",VERTEX,{"derivedFrom":[subQ1,subQ0]});Q30=makeQuery(id+"F4.imprint","IMPRINT",FACE,{"disambiguationData":[TD([[makeQuery(id+"F4.imprint","IMPRINT",EDGE,{"disambiguationData":[TD([[subQ2,-1.0]])],"derivedFrom":subQ1}),-1.0]])]});}
            var Q31;
            {var subQ0=sQuery(id+"F4.wireOp",EDGE,"E16.left");var subQ1=sQuery(id+"F4.wireOp",EDGE,"E16.bottom");var subQ2=makeQuery(id+"F4.imprint","INTERSECT",VERTEX,{"derivedFrom":[subQ1,subQ0]});Q31=makeQuery(id+"F4.imprint","IMPRINT",FACE,{"disambiguationData":[TD([[makeQuery(id+"F4.imprint","IMPRINT",EDGE,{"disambiguationData":[TD([[subQ2,-1.0]])],"derivedFrom":subQ1}),1.0]])]});}
            extrude(context, id + "F5", {"entities" : qUnion([Q0, Q1, Q2, Q3, Q4, Q5, Q6, Q7, Q8, Q9, Q10, Q11, Q12, Q13, Q14, Q15, Q16, Q17, Q18, Q19, Q20, Q21, Q22, Q23, Q24, Q25, Q26, Q27, Q28, Q29, Q30, Q31]), "depth" : 0.76 * mm});
        }
    });
